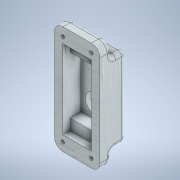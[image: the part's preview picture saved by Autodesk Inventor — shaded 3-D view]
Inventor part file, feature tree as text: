
AUTODESK INVENTOR PART (.ipt)
format: ipt  version: 2021 (Build 250183000, 183)  size: 271,872 bytes
history: native  units: mm
features: extrude x7, sketch x7, fillet x3
ambient origin geometry x8: Origin, YZ Plane, XZ Plane, XY Plane, X Axis, Y Axis, Z Axis, Center Point
bodies: Solid1 (feature_tree)
feature tree (17):
  extrude  "Extrusion1"  Depth=76.0mm
  fillet  "Fillet1"  Radius=18.0mm
  extrude  "Extrusion2"  Depth=20.0mm
  extrude  "Extrusion3"  Depth=18.0mm
  extrude  "Extrusion4"  Depth=12.5mm TaperAngle=0.0deg
  extrude  "Extrusion5"  Depth=10.0mm
  fillet  "Fillet2"  Radius=10.0mm
  extrude  "Extrusion6"  Depth=7.7mm
  extrude  "Extrusion7"  Depth=2.0mm
  fillet  "Fillet3"  Radius=5.0mm
  sketch  "Sketch1"  dims[d0=32.0mm d1=76.0mm d2=18.0mm d3=0.0mm]
  sketch  "Sketch2"  dims[d4=6.0mm d5=20.0mm]
  sketch  "Sketch3"  dims[d6=40.0mm d7=18.0mm]
  sketch  "Sketch4"  dims[d8=6.0mm d9=12.5mm d10=0.0mm]
  sketch  "Sketch5"  dims[d11=13.5mm d12=10.0mm d13=10.0mm]
  sketch  "Sketch6"  dims[d14=12.5mm d15=0.0mm d16=7.7mm]
  sketch  "Sketch7"  dims[d17=20.0mm d18=7.7mm d19=5.0mm d20=0.0mm d21=10.0mm d22=10.0mm d23=10.0mm d24=10.0mm d25=5.0mm d26=0.0mm d27=3.0mm d28=2.4mm d29=2.4mm d30=2.4mm d31=2.4mm d32=5.0mm d33=10.0mm d34=0.0mm d35=0.0mm d36=22.0mm d37=2.0mm d38=0.0mm d39=2.0mm]
